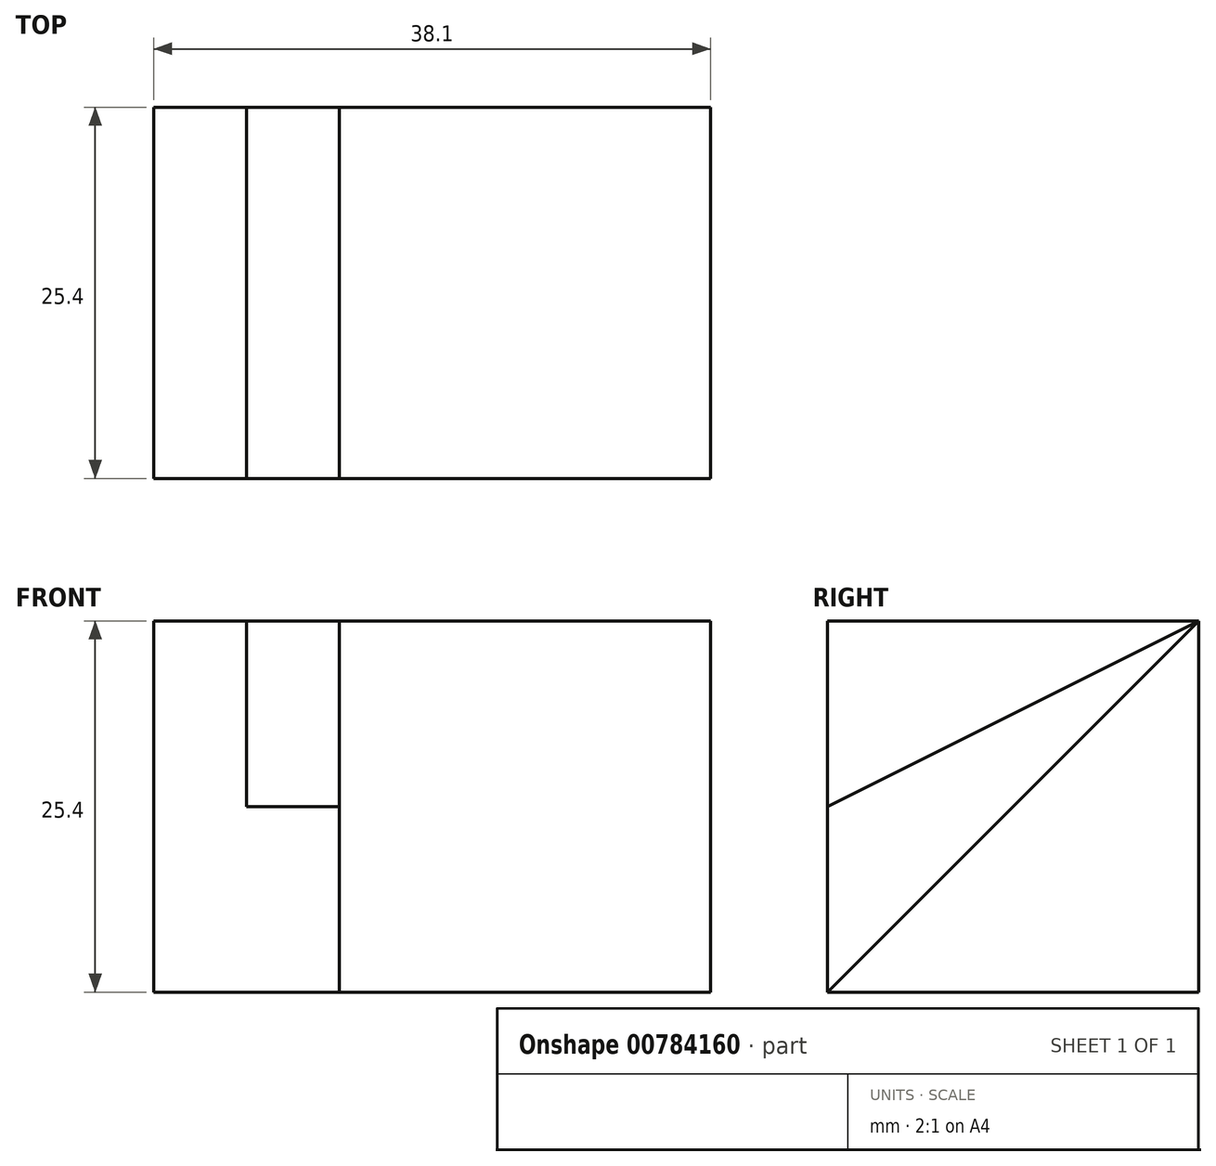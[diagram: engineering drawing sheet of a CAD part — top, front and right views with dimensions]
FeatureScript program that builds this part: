
annotation { "Feature Type Name" : "Feature", "Feature Type Description" : "" }
export const myFeature = defineFeature(function(context is Context, id is Id, definition is map)
    precondition{}
    {
        {
            var Q0;
            Q0=qCreatedBy(makeId("Right.planeOp"),FACE);
            var sketch = newSketch(context, id + "F0", { "sketchPlane" : qUnion([Q0])});
            skLineSegment(sketch, "E0", {"start": v(0, 0) * mm, "end": v(25.4, 0) * mm});
            skLineSegment(sketch, "E1", {"start": v(25.4, 0) * mm, "end": v(25.4, 25.4) * mm});
            skLineSegment(sketch, "E2", {"start": v(25.4, 25.4) * mm, "end": v(0, 25.4) * mm});
            skLineSegment(sketch, "E3", {"start": v(0, 25.4) * mm, "end": v(0, 0) * mm});
            skSolve(sketch);
        }
        {
            var Q0;
            Q0 = qSketchRegion(id + "F0", true);
            extrude(context, id + "F1", {"entities" : qUnion([Q0]), "depth" : 38.1 * mm, "offsetDistance" : 25.4 * mm});
        }
        {
            var Q0;
            Q0=makeQuery(id+"F1.opExtrude","CAP_FACE",FACE,{"disambiguationData":[OSD([sQuery(id+"F0.wireOp",EDGE,"E0"),sQuery(id+"F0.wireOp",EDGE,"E1"),sQuery(id+"F0.wireOp",EDGE,"E2"),sQuery(id+"F0.wireOp",EDGE,"E3")])],"isStart":false});
            var sketch = newSketch(context, id + "F2", { "sketchPlane" : qUnion([Q0])});
            skLineSegment(sketch, "E4", {"start": v(0, 0) * mm, "end": v(25.4, 25.4) * mm});
            skSolve(sketch);
        }
        {
            var Q0;
            Q0=makeQuery(id+"F2.imprint","IMPRINT",FACE,{"disambiguationData":[TD([[makeQuery(id+"F2.imprint","IMPRINT",EDGE,{"derivedFrom":sQuery(id+"F2.wireOp",EDGE,"E4")}),1.0]])]});
            extrude(context, id + "F3", {"entities" : qUnion([Q0]), "operationType" : NewBodyOperationType.REMOVE, "oppositeDirection" : true, "depth" : 25.4 * mm, "offsetDistance" : 25.4 * mm});
        }
        {
            var Q0;
            Q0=makeQuery(id+"F3.boolean.opBoolean","COPY",FACE,{"derivedFrom":makeQuery(id+"F3.opExtrude","CAP_FACE",FACE,{"disambiguationData":[OSD([sQuery(id+"F0.wireOp",EDGE,"E2"),sQuery(id+"F0.wireOp",EDGE,"E3"),sQuery(id+"F2.wireOp",EDGE,"E4")])],"isStart":false})});
            var sketch = newSketch(context, id + "F4", { "sketchPlane" : qUnion([Q0])});
            skLineSegment(sketch, "E5", {"start": v(0, 12.7) * mm, "end": v(25.4, 25.4) * mm});
            skSolve(sketch);
        }
        {
            var Q0;
            {var subQ0=sQuery(id+"F4.wireOp",EDGE,"E5");Q0=makeQuery(id+"F4.imprint","IMPRINT",FACE,{"disambiguationData":[TD([[makeQuery(id+"F4.imprint","IMPRINT",EDGE,{"derivedFrom":subQ0}),1.0]])]});}
            extrude(context, id + "F5", {"entities" : qUnion([Q0]), "operationType" : NewBodyOperationType.REMOVE, "oppositeDirection" : true, "depth" : 6.35 * mm, "offsetDistance" : 25.4 * mm});
        }
    });
